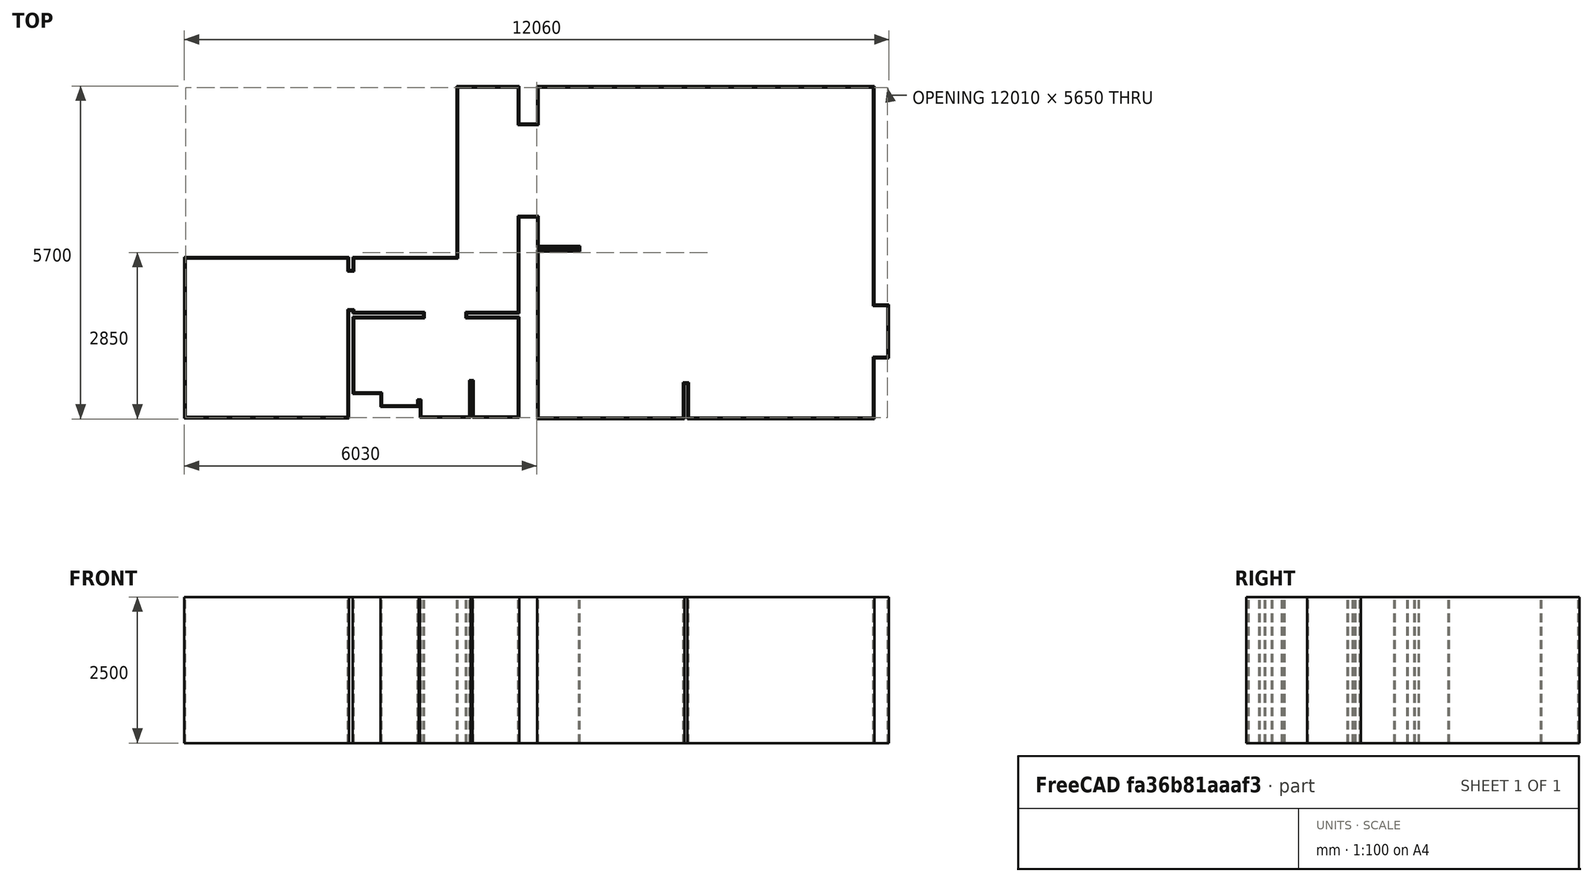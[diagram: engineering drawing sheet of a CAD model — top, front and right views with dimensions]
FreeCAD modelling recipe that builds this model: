
FCSTD DOCUMENT  (FreeCAD 0.18.4R)
Label: apartment
License: All rights reserved
LicenseURL: http://en.wikipedia.org/wiki/All_rights_reserved
objects: Sketcher::SketchObject×1, Part::Part2DObjectPython×1, Part::FeaturePython×1, App::Part×1
note: 3 computed .brp shape members not serialized (recipe doc carries the construction recipe); baked Part::Feature solids carry a one-line shape summary decoded from their .brp

FEATURE [Sketcher::SketchObject] Sketch
  MapMode = 5
  Support = -> [XY_Plane001]
  sketch-geometry (52):
    g0: LineSegment StartX=0 StartY=0 StartZ=0 EndX=1020 EndY=0 EndZ=0
    g1: LineSegment StartX=1020 StartY=0 StartZ=0 EndX=1020 EndY=-640 EndZ=0
    g2: LineSegment StartX=1020 StartY=-640 StartZ=0 EndX=1380 EndY=-640 EndZ=0
    g3: LineSegment StartX=1380 StartY=-640 StartZ=0 EndX=1380 EndY=0 EndZ=0
    g4: LineSegment StartX=1380 StartY=0 StartZ=0 EndX=7100 EndY=0 EndZ=0
    g5: LineSegment StartX=7100 StartY=0 StartZ=0 EndX=7100 EndY=-3740 EndZ=0
    g6: LineSegment StartX=7100 StartY=-3740 StartZ=0 EndX=7350 EndY=-3740 EndZ=0
    g7: LineSegment StartX=7350 StartY=-3740 StartZ=0 EndX=7350 EndY=-4610 EndZ=0
    g8: LineSegment StartX=7100 StartY=-4610 StartZ=0 EndX=7350 EndY=-4610 EndZ=0
    g9: LineSegment StartX=7100 StartY=-4610 StartZ=0 EndX=7100 EndY=-5650 EndZ=0
    g10: LineSegment StartX=3950 StartY=-5650 StartZ=0 EndX=7100 EndY=-5650 EndZ=0
    g11: LineSegment StartX=3950 StartY=-5050 StartZ=0 EndX=3950 EndY=-5650 EndZ=0
    g12: LineSegment StartX=3850 StartY=-5050 StartZ=0 EndX=3950 EndY=-5050 EndZ=0
    g13: LineSegment StartX=3850 StartY=-5050 StartZ=0 EndX=3850 EndY=-5650 EndZ=0
    g14: LineSegment StartX=1380 StartY=-5650 StartZ=0 EndX=3850 EndY=-5650 EndZ=0
    g15: LineSegment StartX=1380 StartY=-2810 StartZ=0 EndX=1380 EndY=-5650 EndZ=0
    g16: LineSegment StartX=1380 StartY=-2810 StartZ=0 EndX=2090 EndY=-2810 EndZ=0
    g17: LineSegment StartX=2090 StartY=-2810 StartZ=0 EndX=2090 EndY=-2710 EndZ=0
    g18: LineSegment StartX=1380 StartY=-2710 StartZ=0 EndX=2090 EndY=-2710 EndZ=0
    g19: LineSegment StartX=1020 StartY=-2200 StartZ=0 EndX=1380 EndY=-2200 EndZ=0
    g20: LineSegment StartX=1380 StartY=-2710 StartZ=0 EndX=1380 EndY=-2200 EndZ=0
    g21: LineSegment StartX=0 StartY=0 StartZ=0 EndX=0 EndY=-2930 EndZ=0
    g22: LineSegment StartX=-1780 StartY=-2930 StartZ=0 EndX=0 EndY=-2930 EndZ=0
    g23: LineSegment StartX=1020 StartY=-2200 StartZ=0 EndX=1020 EndY=-3840 EndZ=0
    g24: LineSegment StartX=1020 StartY=-3840 StartZ=0 EndX=130 EndY=-3840 EndZ=0
    g25: LineSegment StartX=130 StartY=-3840 StartZ=0 EndX=130 EndY=-3950 EndZ=0
    g26: LineSegment StartX=130 StartY=-3950 StartZ=0 EndX=1020 EndY=-3950 EndZ=0
    g27: LineSegment StartX=1020 StartY=-3950 StartZ=0 EndX=1020 EndY=-5630 EndZ=0
    g28: LineSegment StartX=1020 StartY=-5630 StartZ=0 EndX=270 EndY=-5630 EndZ=0
    g29: LineSegment StartX=270 StartY=-5010 StartZ=0 EndX=270 EndY=-5630 EndZ=0
    g30: LineSegment StartX=190 StartY=-5010 StartZ=0 EndX=270 EndY=-5010 EndZ=0
    g31: LineSegment StartX=190 StartY=-5010 StartZ=0 EndX=190 EndY=-5630 EndZ=0
    g32: LineSegment StartX=190 StartY=-5630 StartZ=0 EndX=-630 EndY=-5630 EndZ=0
    g33: LineSegment StartX=-630 StartY=-5630 StartZ=0 EndX=-630 EndY=-5340 EndZ=0
    g34: LineSegment StartX=-630 StartY=-5340 StartZ=0 EndX=-700 EndY=-5340 EndZ=0
    g35: LineSegment StartX=-700 StartY=-5340 StartZ=0 EndX=-700 EndY=-5440 EndZ=0
    g36: LineSegment StartX=-700 StartY=-5440 StartZ=0 EndX=-1300 EndY=-5440 EndZ=0
    g37: LineSegment StartX=-1300 StartY=-5440 StartZ=0 EndX=-1300 EndY=-5220 EndZ=0
    g38: LineSegment StartX=-1300 StartY=-5220 StartZ=0 EndX=-1780 EndY=-5220 EndZ=0
    g39: LineSegment StartX=-1780 StartY=-5220 StartZ=0 EndX=-1780 EndY=-3950 EndZ=0
    g40: LineSegment StartX=-1780 StartY=-3950 StartZ=0 EndX=-570 EndY=-3950 EndZ=0
    g41: LineSegment StartX=-570 StartY=-3950 StartZ=0 EndX=-570 EndY=-3840 EndZ=0
    g42: LineSegment StartX=-570 StartY=-3840 StartZ=0 EndX=-1780 EndY=-3840 EndZ=0
    g43: LineSegment StartX=-1780 StartY=-3840 StartZ=0 EndX=-1780 EndY=-3800 EndZ=0
    g44: LineSegment StartX=-1780 StartY=-3800 StartZ=0 EndX=-1890 EndY=-3800 EndZ=0
    g45: LineSegment StartX=-1890 StartY=-3800 StartZ=0 EndX=-1890 EndY=-5640 EndZ=0
    g46: LineSegment StartX=-1890 StartY=-5640 StartZ=0 EndX=-4660 EndY=-5640 EndZ=0
    g47: LineSegment StartX=-4660 StartY=-2930 StartZ=0 EndX=-1890 EndY=-2930 EndZ=0
    g48: LineSegment StartX=-1890 StartY=-2930 StartZ=0 EndX=-1890 EndY=-3150 EndZ=0
    g49: LineSegment StartX=-1890 StartY=-3150 StartZ=0 EndX=-1780 EndY=-3150 EndZ=0
    g50: LineSegment StartX=-1780 StartY=-3150 StartZ=0 EndX=-1780 EndY=-2930 EndZ=0
    g51: LineSegment StartX=-4660 StartY=-2930 StartZ=0 EndX=-4660 EndY=-5640 EndZ=0
  constraints (206):
    c: Coincident(g0,g-1)
    c: Horizontal(g0)
    c: Distance(g0) = 1020
    c: Coincident(g1,g0)
    c: Vertical(g1)
    c: Distance(g1) = 640
    c: Coincident(g2,g1)
    c: Horizontal(g2)
    c: Distance(g2) = 360
    c: Coincident(g3,g2)
    c: Vertical(g3)
    c: Distance(g3) = 640
    c: Horizontal(g4)
    c: Distance(g4) = 5720
    c: Coincident(g3,g4)
    c: Block(g3)
    c: Block(g2)
    c: Block(g1)
    c: Block(g0)
    c: Block(g4)
    c: Vertical(g5)
    c: Coincident(g5,g4)
    c: Distance(g5) = 3740
    c: Block(g5)
    c: Horizontal(g6)
    c: Coincident(g6,g5)
    c: Distance(g6) = 250
    c: Block(g6)
    c: Coincident(g7,g6)
    c: Vertical(g7)
    c: Distance(g7) = 870
    c: Block(g7)
    c: Coincident(g8,g7)
    c: Horizontal(g8)
    c: Distance(g8) = 250
    c: Block(g8)
    c: Coincident(g8,g9)
    c: Vertical(g9)
    c: Distance(g9) = 1040
    c: Block(g9)
    c: Coincident(g10,g9)
    c: Horizontal(g10)
    c: Distance(g10) = 3150
    c: Block(g10)
    c: Coincident(g11,g10)
    c: Vertical(g11)
    c: Distance(g11) = 600
    c: Block(g11)
    c: Coincident(g12,g11)
    c: Horizontal(g12)
    c: Distance(g12) = 100
    c: Vertical(g13)
    c: Coincident(g13,g12)
    c: Distance(g13) = 600
    c: Block(g12)
    c: Block(g13)
    c: Coincident(g14,g13)
    c: Horizontal(g14)
    c: Distance(g14) = 2470
    c: Coincident(g15,g14)
    c: Vertical(g15)
    c: Coincident(g16,g15)
    c: Coincident(g16,g17)
    c: Horizontal(g16)
    c: Vertical(g17)
    c: Horizontal(g18)
    c: Distance(g18) = 710
    c: Coincident(g18,g17)
    c: Horizontal(g19)
    c: Distance(g19) = 360
    c: Block(g14)
    c: Distance(g15) = 2840
    c: Distance(g16) = 710
    c: Distance(g17) = 100
    c: Coincident(g20,g18)
    c: Coincident(g19,g20)
    c: Distance(g20) = 510
    c: Block(g15)
    c: Block(g16)
    c: Block(g17)
    c: Block(g18)
    c: Block(g20)
    c: Block(g19)
    c: Coincident(g21,g0)
    c: Vertical(g21)
    c: Distance(g21) = 2930
    c: Coincident(g22,g21)
    c: Horizontal(g22)
    c: Distance(g22) = 1780
    c: Coincident(g23,g19)
    c: Vertical(g23)
    c: Distance(g23) = 1640
    c: Block(g21)
    c: Block(g22)
    c: Block(g23)
    c: Coincident(g23,g24)
    c: Horizontal(g24)
    c: Distance(g24) = 890
    c: Coincident(g25,g24)
    c: Vertical(g25)
    c: Distance(g25) = 110
    c: Coincident(g26,g25)
    c: Horizontal(g26)
    c: Distance(g26) = 890
    c: Coincident(g27,g26)
    c: Vertical(g27)
    c: Distance(g27) = 1680
    c: Coincident(g28,g27)
    c: Horizontal(g28)
    c: Distance(g28) = 750
    c: Coincident(g29,g28)
    c: Vertical(g29)
    c: Distance(g29) = 620
    c: Coincident(g30,g29)
    c: Horizontal(g30)
    c: Distance(g30) = 80
    c: Block(g24)
    c: Block(g25)
    c: Block(g26)
    c: Block(g27)
    c: Block(g28)
    c: Block(g29)
    c: Block(g30)
    c: Coincident(g31,g30)
    c: Vertical(g31)
    c: Distance(g31) = 620
    c: Coincident(g32,g33)
    c: Coincident(g33,g34)
    c: Coincident(g34,g35)
    c: Coincident(g35,g36)
    c: Coincident(g36,g37)
    c: Coincident(g37,g38)
    c: Coincident(g38,g39)
    c: Coincident(g39,g40)
    c: Coincident(g40,g41)
    c: Coincident(g41,g42)
    c: Coincident(g42,g43)
    c: Coincident(g43,g44)
    c: Coincident(g44,g45)
    c: Coincident(g45,g46)
    c: Coincident(g47,g48)
    c: Coincident(g48,g49)
    c: Coincident(g49,g50)
    c: Block(g31)
    c: Coincident(g32,g31)
    c: Horizontal(g32)
    c: Vertical(g33)
    c: Horizontal(g34)
    c: Horizontal(g36)
    c: Horizontal(g38)
    c: Vertical(g35)
    c: Vertical(g37)
    c: Vertical(g39)
    c: Vertical(g41)
    c: Horizontal(g40)
    c: Horizontal(g42)
    c: Horizontal(g44)
    c: Vertical(g43)
    c: Vertical(g45)
    c: Horizontal(g46)
    c: Horizontal(g47)
    c: Horizontal(g49)
    c: Vertical(g48)
    c: Vertical(g50)
    c: Distance(g32) = 820
    c: Distance(g33) = 290
    c: Distance(g34) = 70
    c: Distance(g35) = 100
    c: Distance(g36) = 600
    c: Distance(g37) = 220
    c: Distance(g38) = 480
    c: Distance(g39) = 1270
    c: Distance(g40) = 1210
    c: Distance(g41) = 110
    c: Distance(g42) = 1210
    c: Distance(g43) = 40
    c: Distance(g44) = 110
    c: Distance(g45) = 1840
    c: Block(g32)
    c: Block(g33)
    c: Block(g34)
    c: Block(g35)
    c: Block(g36)
    c: Block(g37)
    c: Block(g38)
    c: Block(g39)
    c: Block(g40)
    c: Block(g41)
    c: Distance(g46) = 2770
    c: Coincident(g50,g22)
    c: Distance(g50) = 220
    c: Distance(g49) = 110
    c: Distance(g48) = 220
    c: Block(g50)
    c: Block(g49)
    c: Block(g48)
    c: Block(g42)
    c: Block(g43)
    c: Block(g44)
    c: Block(g45)
    c: Coincident(g51,g47)
    c: Coincident(g51,g46)
    c: Vertical(g51)
    c: Block(g47)
    c: Block(g46)
    c: Block(g51)
FEATURE [Part::Part2DObjectPython] Wire  # Draft 2D object (typed FeaturePython)
  ChamferSize = 0
  Closed = true
  End = (-12.5,-2917.5,0)
  FilletRadius = 0
  Length = 55940
  MakeFace = false
  Points = (52) [(-12.5,12.5,0),(1032.5,12.5,0),(1032.5,-627.5,0),(1367.5,-627.5,0),(1367.5,12.5,0),(7112.5,12.5,0),(7112.5,-3727.5,0),(7362.5,-3727.5,0),+44 more]
  Start = (-12.5,12.5,0)
  Subdivisions = 0
FEATURE [Part::FeaturePython] Wall  # Arch/BIM object (typed FeaturePython)
  Align = 2
  Base = -> Wire
  BlockHeight = 0
  BlockLength = 0
  CountBroken = 0
  CountEntire = 0
  Face = 0
  Height = 2500
  HorizontalArea = 0
  IfcRole = 156
  Joint = 0
  Length = 55940
  MakeBlocks = false
  MoveWithHost = false
  Normal = (0,0,0)
  OffsetFirst = 0
  OffsetSecond = 0
  PerimeterLength = 0
  VerticalArea = 0
  Width = 25
FEATURE [App::Part] Part  label="walls"
  Group = -> [Sketch,Wire,Wall]
  Origin = -> Origin001
